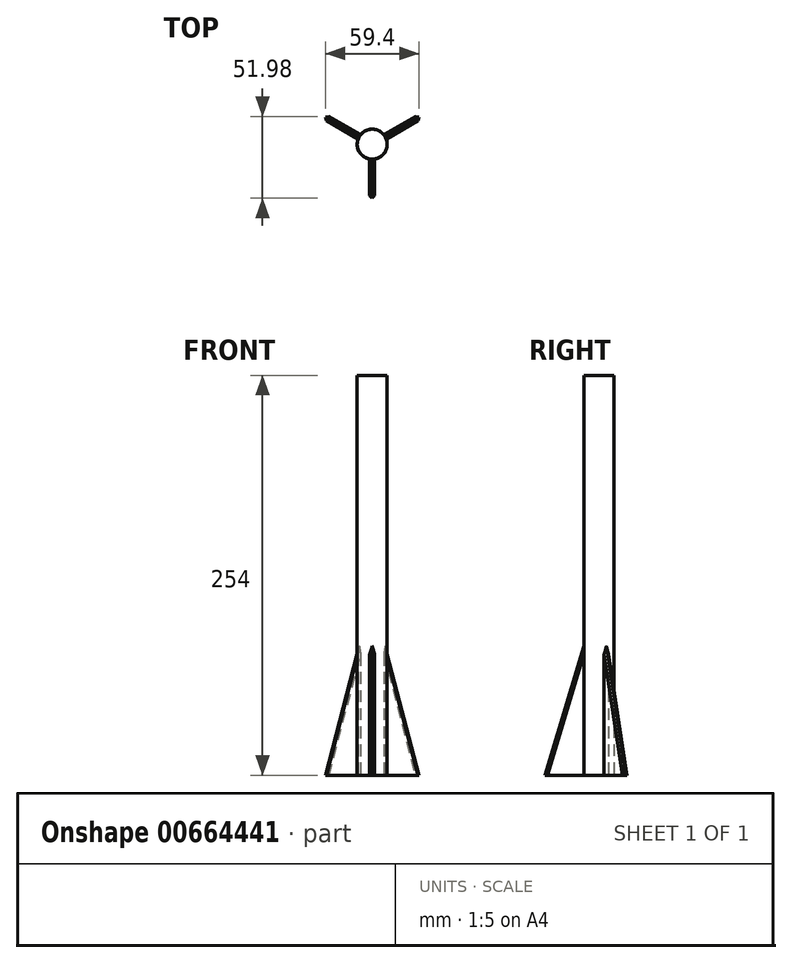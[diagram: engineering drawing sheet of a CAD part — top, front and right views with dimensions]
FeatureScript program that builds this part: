
annotation { "Feature Type Name" : "Feature", "Feature Type Description" : "" }
export const myFeature = defineFeature(function(context is Context, id is Id, definition is map)
    precondition{}
    {
        {
            var Q0;
            Q0=qCreatedBy(makeId("Top.planeOp"),FACE);
            var sketch = newSketch(context, id + "F0", { "sketchPlane" : qUnion([Q0])});
            skCircle(sketch, "E0", {"center": v(0, 0) * mm, "radius": 9.53 * mm});
            skSolve(sketch);
        }
        {
            var Q0;
            Q0 = qSketchRegion(id + "F0", true);
            extrude(context, id + "F1", {"entities" : qUnion([Q0]), "depth" : 254 * mm, "offsetDistance" : 25.4 * mm});
        }
        {
            var Q0;
            Q0=qCreatedBy(makeId("Right.planeOp"),FACE);
            var sketch = newSketch(context, id + "F2", { "sketchPlane" : qUnion([Q0])});
            skLineSegment(sketch, "E1", {"start": v(-9.53, 0) * mm, "end": v(-9.53, 254) * mm});
            skLineSegment(sketch, "E2", {"start": v(9.53, 254) * mm, "end": v(9.53, 0) * mm});
            skLineSegment(sketch, "E3", {"start": v(-9.53, 83.56) * mm, "end": v(-34.76, 0) * mm});
            skLineSegment(sketch, "E4", {"start": v(-34.76, 0) * mm, "end": v(-9.53, 0) * mm});
            skLineSegment(sketch, "E5", {"start": v(-9.52, 83.56) * mm, "end": v(-6.31, 83.56) * mm});
            skLineSegment(sketch, "E6", {"start": v(-6.31, 83.56) * mm, "end": v(-6.31, 0) * mm});
            skLineSegment(sketch, "E7", {"start": v(-6.31, 0) * mm, "end": v(-9.53, 0) * mm});
            skSolve(sketch);
        }
        {
            var Q0;
            Q0 = qSketchRegion(id + "F2", true);
            extrude(context, id + "F3", {"entities" : qUnion([Q0]), "operationType" : NewBodyOperationType.ADD, "endBound" : BoundingType.SYMMETRIC, "depth" : 3.17 * mm, "offsetDistance" : 25.4 * mm});
        }
        {
            var Q0;
            Q0=makeQuery(id+"F3.opExtrude","CAP_EDGE",EDGE,{"disambiguationData":[OSD([sQuery(id+"F2.wireOp",EDGE,"E3")])],"isStart":false});
            var Q1;
            Q1=makeQuery(id+"F3.opExtrude","CAP_EDGE",EDGE,{"disambiguationData":[OSD([sQuery(id+"F2.wireOp",EDGE,"E3")])],"isStart":true});
            chamfer(context, id + "F4", {"entities" : qUnion([Q0, Q1]), "width" : 2.03 * mm, "tangentPropagation" : true});
        }
        {
            var Q0;
            Q0=makeQuery(id+"F1.opExtrude","SWEPT_BODY",BODY,{"disambiguationData":[OSD([sQuery(id+"F0.wireOp",EDGE,"E0")])]});
            var Q1;
            Q1=makeQuery(id+"F1.opExtrude","SWEPT_FACE",FACE,{"disambiguationData":[OSD([sQuery(id+"F0.wireOp",EDGE,"E0")])]});
            circularPattern(context, id + "F5", {"entities" : qUnion([Q0]), "axis" : qUnion([Q1]), "angle" : 360 * degree, "instanceCount" : 3, "equalSpace" : true});
        }
    });
